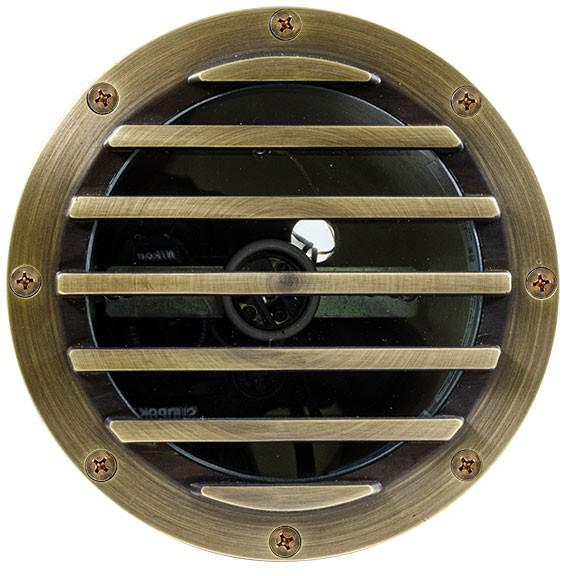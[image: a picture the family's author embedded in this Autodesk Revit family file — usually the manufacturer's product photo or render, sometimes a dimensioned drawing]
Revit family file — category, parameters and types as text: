
# Revit family: Alcon-9045-Revit-Family
name_source: partatom
category: Luminarias
units: mm (PartAtom-declared; Revit-internal decimal feet)

## family parameters
Anfitrión = Cara
Compartido = No
Corte con vacíos al cargar = No
Cota de conector redondo = Usar diámetro
Mantener orientación de anotación = No
Origen de luz = Sí
Punto de cálculo de habitación = No
Tipo de pieza = Normal

## types (1)
- Alcon-9045-Revit-Family
    Cambio de temperatura de color de luz atenuada = <Ninguno>
    Elevación por defecto = 4' - 0"
    Fabricante = Alcon Lighting
    Filtro de color = 16777215
    LENS GLASS = Glass
    Link to IES File = https://www.alconlighting.com
    Longitud de símbolo de origen de luz = 10' - 0"
    Modelo = Alcon Lighting 9045
    Product Data URL = https://www.alconlighting.com
    Product Page = https://www.alconlighting.com
    TOP FINISH = <Por categoría>
    URL = https://www.alconlighting.com
    Ángulo de campo de foco = 90.00°
    Ángulo de enfoque = 30.00°
    Ángulo de inclinación = 60.00°

## geometry (parser evidence)
native form markers: Sweep x3
no freeform markers — native parametric forms only
